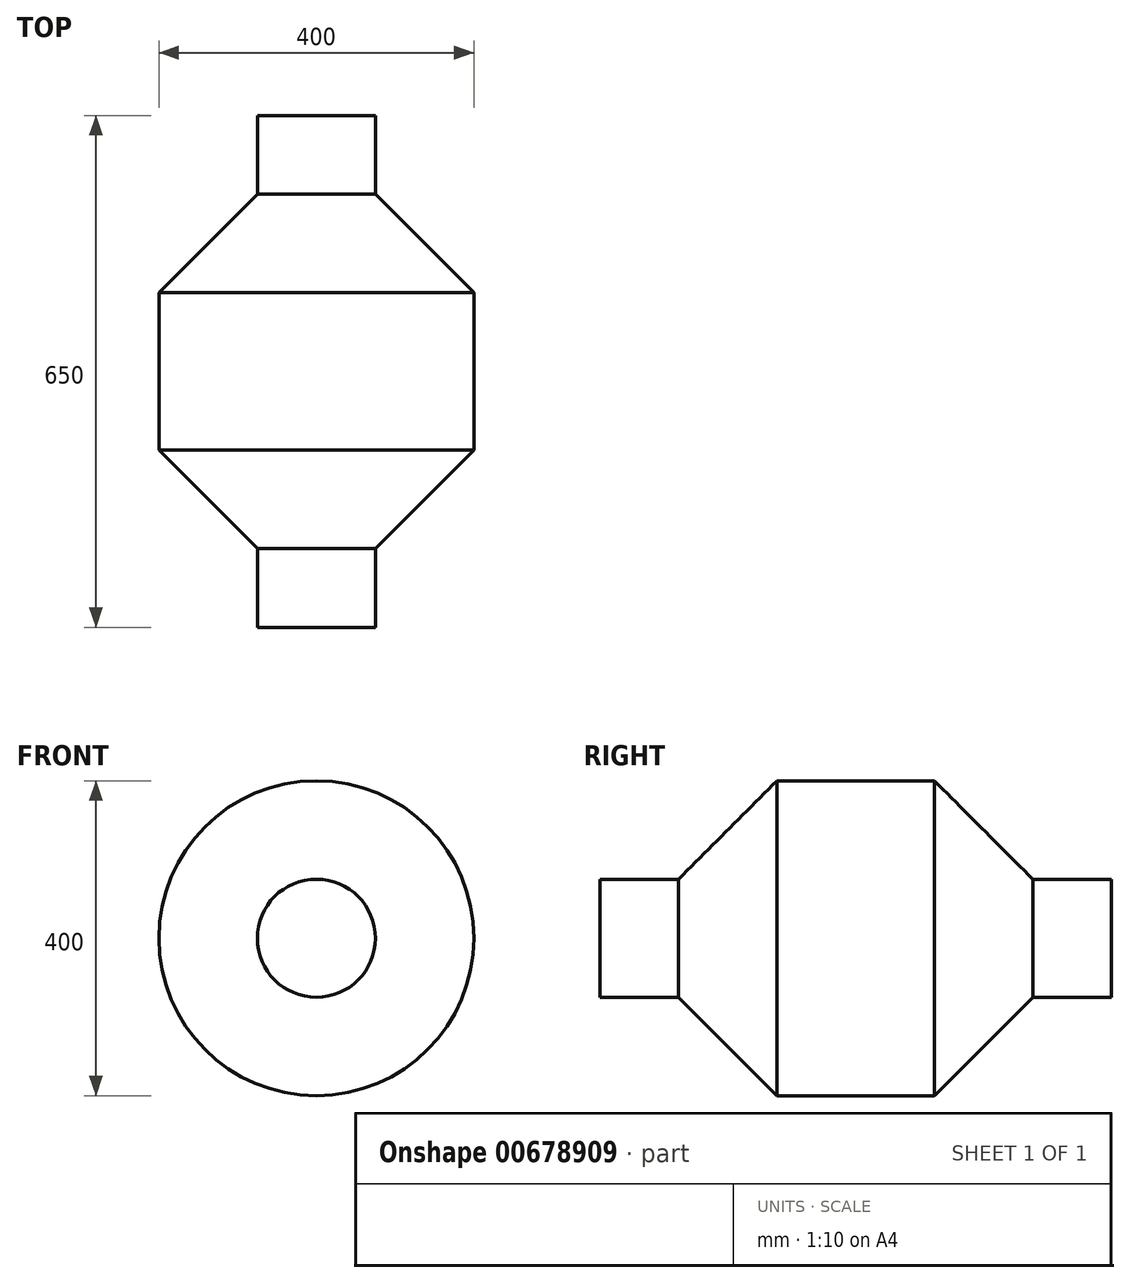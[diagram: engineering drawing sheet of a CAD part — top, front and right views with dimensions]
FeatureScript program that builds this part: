
annotation { "Feature Type Name" : "Feature", "Feature Type Description" : "" }
export const myFeature = defineFeature(function(context is Context, id is Id, definition is map)
    precondition{}
    {
        {
            var Q0;
            Q0=qCreatedBy(makeId("Right.planeOp"),FACE);
            var sketch = newSketch(context, id + "F0", { "sketchPlane" : qUnion([Q0])});
            skLineSegment(sketch, "E0", {"start": v(0, 0) * mm, "end": v(0, 75) * mm});
            skLineSegment(sketch, "E1", {"start": v(0, 75) * mm, "end": v(100, 75) * mm});
            skLineSegment(sketch, "E2", {"start": v(100, 75) * mm, "end": v(225, 200) * mm});
            skLineSegment(sketch, "E3", {"start": v(225, 200) * mm, "end": v(425, 200) * mm});
            skLineSegment(sketch, "E4", {"start": v(425, 200) * mm, "end": v(550, 75) * mm});
            skLineSegment(sketch, "E5", {"start": v(550, 75) * mm, "end": v(650, 75) * mm});
            skLineSegment(sketch, "E6", {"start": v(650, 75) * mm, "end": v(650, 0) * mm});
            skLineSegment(sketch, "E7", {"start": v(650, 0) * mm, "end": v(0, 0) * mm});
            skSolve(sketch);
        }
        {
            var Q0;
            Q0=makeQuery(id+"F0.imprint","IMPRINT",FACE,{"disambiguationData":[TD([[makeQuery(id+"F0.imprint","IMPRINT",EDGE,{"derivedFrom":sQuery(id+"F0.wireOp",EDGE,"E0")}),-1.0]])]});
            var Q1;
            Q1=sQuery(id+"F0.wireOp",EDGE,"E7");
            revolve(context, id + "F1", {"entities" : qUnion([Q0]), "axis" : qUnion([Q1]), "revolveType" : RevolveType.FULL});
        }
    });
